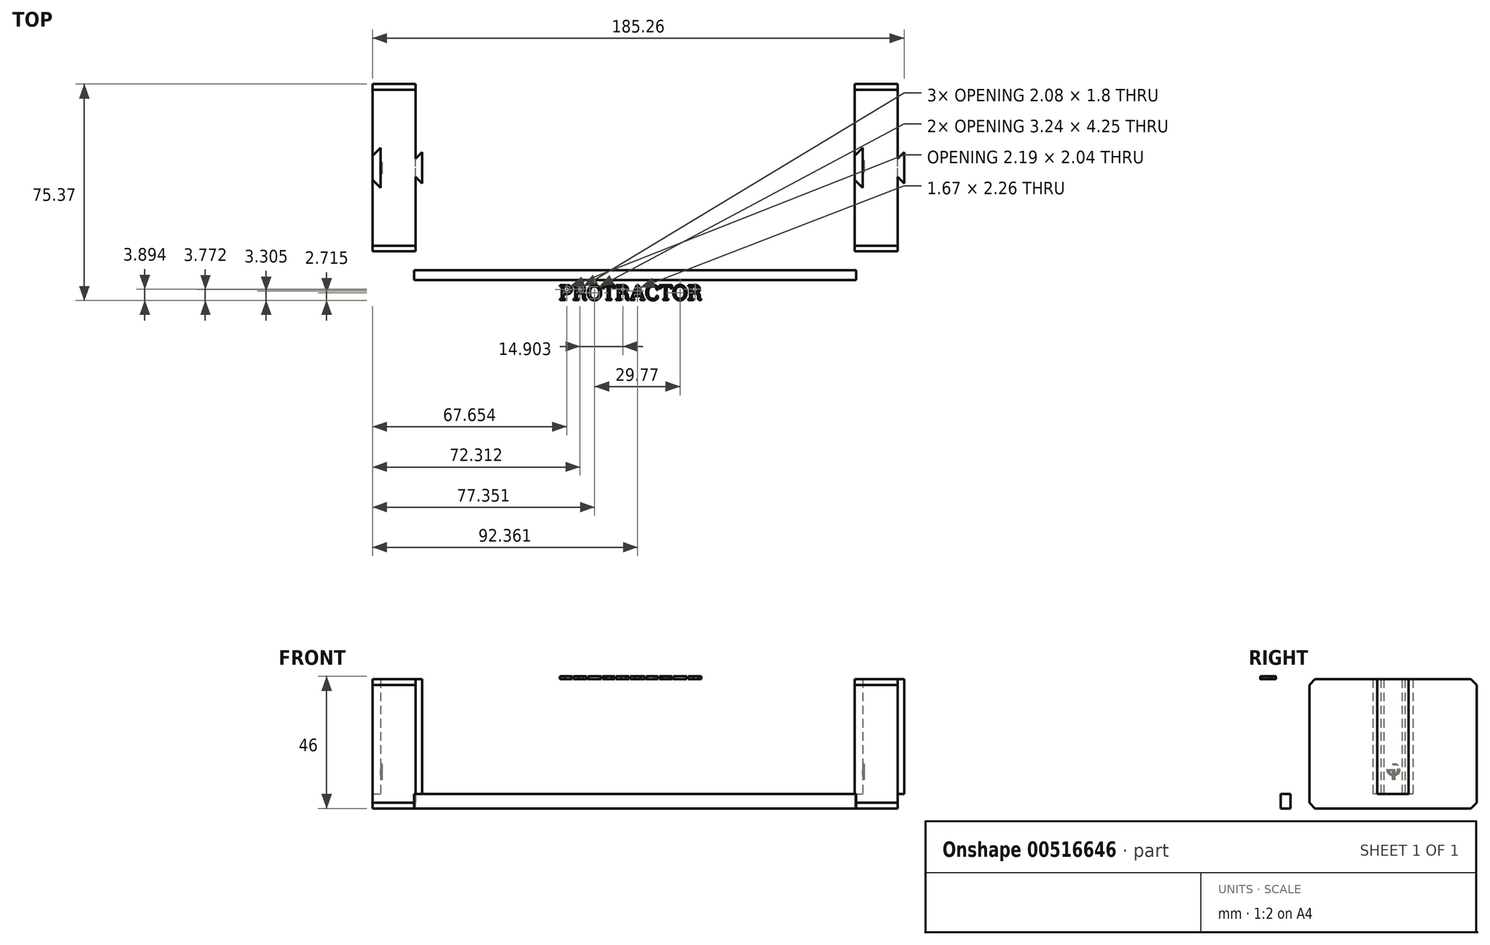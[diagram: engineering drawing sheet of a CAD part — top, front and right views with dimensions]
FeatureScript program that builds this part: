
annotation { "Feature Type Name" : "Feature", "Feature Type Description" : "" }
export const myFeature = defineFeature(function(context is Context, id is Id, definition is map)
    precondition{}
    {
        {
            var Q0;
            Q0=qCreatedBy(makeId("Top.planeOp"),FACE);
            var sketch = newSketch(context, id + "F0", { "sketchPlane" : qUnion([Q0])});
            skLineSegment(sketch, "E0", {"start": v(-15, 4.17) * mm, "end": v(-15, 29.17) * mm});
            skLineSegment(sketch, "E1", {"start": v(-15, 29.17) * mm, "end": v(0, 29.17) * mm});
            skLineSegment(sketch, "E2", {"start": v(0, 29.17) * mm, "end": v(0, 3.17) * mm});
            skLineSegment(sketch, "E3", {"start": v(-15, 4.17) * mm, "end": v(-12.17, 7) * mm});
            skLineSegment(sketch, "E4", {"start": v(-12.17, 7) * mm, "end": v(-12.17, 0) * mm});
            skLineSegment(sketch, "E5", {"start": v(0, 3.17) * mm, "end": v(2.26, 5.43) * mm});
            skLineSegment(sketch, "E6", {"start": v(2.26, 5.43) * mm, "end": v(2.26, -0.57) * mm});
            skLineSegment(sketch, "E7.MirrorCS", {"start": v(-15, -4.12) * mm, "end": v(-12.17, -6.95) * mm});
            skLineSegment(sketch, "E8.MirrorCS", {"start": v(0, -29.12) * mm, "end": v(0, -3.12) * mm});
            skLineSegment(sketch, "E9.MirrorCS", {"start": v(-12.17, -6.95) * mm, "end": v(-12.17, 0.05) * mm});
            skLineSegment(sketch, "E10.MirrorCS", {"start": v(-15, -4.12) * mm, "end": v(-15, -29.12) * mm});
            skLineSegment(sketch, "E11.MirrorCS", {"start": v(2.26, -5.39) * mm, "end": v(2.26, 0.61) * mm});
            skLineSegment(sketch, "E12.MirrorCS", {"start": v(0, -3.12) * mm, "end": v(2.26, -5.39) * mm});
            skLineSegment(sketch, "E13", {"start": v(153, 4.17) * mm, "end": v(153, 29.17) * mm});
            skLineSegment(sketch, "E14", {"start": v(153, 29.17) * mm, "end": v(168, 29.17) * mm});
            skLineSegment(sketch, "E15", {"start": v(168, 29.17) * mm, "end": v(168, 3.17) * mm});
            skLineSegment(sketch, "E16", {"start": v(153, 4.17) * mm, "end": v(155.83, 7) * mm});
            skLineSegment(sketch, "E17", {"start": v(155.83, 7) * mm, "end": v(155.83, 0) * mm});
            skLineSegment(sketch, "E18", {"start": v(168, 3.17) * mm, "end": v(170.26, 5.43) * mm});
            skLineSegment(sketch, "E19", {"start": v(170.26, 5.43) * mm, "end": v(170.26, -0.57) * mm});
            skLineSegment(sketch, "E20.MirrorCS", {"start": v(153, -4.17) * mm, "end": v(155.83, -7) * mm});
            skLineSegment(sketch, "E21.MirrorCS", {"start": v(168, -29.17) * mm, "end": v(168, -3.17) * mm});
            skLineSegment(sketch, "E22.MirrorCS", {"start": v(155.83, -7) * mm, "end": v(155.83, 0) * mm});
            skLineSegment(sketch, "E23.MirrorCS", {"start": v(153, -4.17) * mm, "end": v(153, -29.17) * mm});
            skLineSegment(sketch, "E24.MirrorCS", {"start": v(170.26, -5.43) * mm, "end": v(170.26, 0.57) * mm});
            skLineSegment(sketch, "E25.MirrorCS", {"start": v(168, -3.17) * mm, "end": v(170.26, -5.43) * mm});
            skLineSegment(sketch, "E26.bottom", {"start": v(-15, -29.12) * mm, "end": v(168, -29.12) * mm});
            skLineSegment(sketch, "E26.top", {"start": v(-15, -49.12) * mm, "end": v(168, -49.12) * mm});
            skLineSegment(sketch, "E26.left", {"start": v(-15, -29.12) * mm, "end": v(-15, -49.12) * mm});
            skLineSegment(sketch, "E26.right", {"start": v(168, -29.12) * mm, "end": v(168, -49.12) * mm});
            skLineSegment(sketch, "E27.bottom", {"start": v(-0.5, -35.62) * mm, "end": v(153.5, -35.62) * mm});
            skLineSegment(sketch, "E27.top", {"start": v(-0.5, -39.12) * mm, "end": v(153.5, -39.12) * mm});
            skLineSegment(sketch, "E27.left", {"start": v(-0.5, -35.62) * mm, "end": v(-0.5, -39.12) * mm});
            skLineSegment(sketch, "E27.right", {"start": v(153.5, -35.62) * mm, "end": v(153.5, -39.12) * mm});
            skLineSegment(sketch, "E28", {"start": v(-15, 4.17) * mm, "end": v(-15, -4.12) * mm});
            skLineSegment(sketch, "E29", {"start": v(153, -4.17) * mm, "end": v(153, 4.17) * mm});
            skLineSegment(sketch, "E30", {"start": v(0, 3.17) * mm, "end": v(0, -3.12) * mm});
            skLineSegment(sketch, "E31", {"start": v(168, 3.17) * mm, "end": v(168, -3.17) * mm});
            skSolve(sketch);
        }
        {
            var Q0;
            Q0=makeQuery(id+"F0.imprint","IMPRINT",FACE,{"disambiguationData":[TD([[makeQuery(id+"F0.imprint","IMPRINT",EDGE,{"derivedFrom":sQuery(id+"F0.wireOp",EDGE,"E5")}),-1.0]])]});
            var Q1;
            Q1=makeQuery(id+"F0.imprint","IMPRINT",FACE,{"disambiguationData":[TD([[makeQuery(id+"F0.imprint","IMPRINT",EDGE,{"derivedFrom":sQuery(id+"F0.wireOp",EDGE,"E18")}),-1.0]])]});
            var Q2;
            Q2=makeQuery(id+"F0.imprint","IMPRINT",FACE,{"disambiguationData":[TD([[makeQuery(id+"F0.imprint","IMPRINT",EDGE,{"derivedFrom":sQuery(id+"F0.wireOp",EDGE,"E0")}),-1.0]])]});
            var Q3;
            Q3=makeQuery(id+"F0.imprint","IMPRINT",FACE,{"disambiguationData":[TD([[makeQuery(id+"F0.imprint","IMPRINT",EDGE,{"derivedFrom":sQuery(id+"F0.wireOp",EDGE,"E13")}),-1.0]])]});
            var Q4;
            {var subQ0=sQuery(id+"F0.wireOp",EDGE,"E26.top");Q4=makeQuery(id+"F0.imprint","IMPRINT",FACE,{"disambiguationData":[TD([[makeQuery(id+"F0.imprint","IMPRINT",EDGE,{"derivedFrom":subQ0}),1.0]])]});}
            extrude(context, id + "F1", {"entities" : qUnion([Q0, Q1, Q2, Q3, Q4]), "depth" : 40 * mm, "offsetDistance" : 25 * mm});
        }
        {
            var Q0;
            Q0=makeQuery(id+"F0.imprint","IMPRINT",FACE,{"disambiguationData":[TD([[makeQuery(id+"F0.imprint","IMPRINT",EDGE,{"derivedFrom":sQuery(id+"F0.wireOp",EDGE,"E0")}),-1.0]])]});
            var Q1;
            Q1=makeQuery(id+"F0.imprint","IMPRINT",FACE,{"disambiguationData":[TD([[makeQuery(id+"F0.imprint","IMPRINT",EDGE,{"derivedFrom":sQuery(id+"F0.wireOp",EDGE,"E13")}),-1.0]])]});
            var Q2;
            Q2=makeQuery(id+"F0.imprint","IMPRINT",FACE,{"disambiguationData":[TD([[makeQuery(id+"F0.imprint","IMPRINT",EDGE,{"derivedFrom":sQuery(id+"F0.wireOp",EDGE,"E27.bottom")}),-1.0]])]});
            var Q3;
            {var subQ0=sQuery(id+"F0.wireOp",EDGE,"E26.top");Q3=makeQuery(id+"F0.imprint","IMPRINT",FACE,{"disambiguationData":[TD([[makeQuery(id+"F0.imprint","IMPRINT",EDGE,{"derivedFrom":subQ0}),1.0]])]});}
            var Q4;
            Q4=makeQuery(id+"F0.imprint","IMPRINT",FACE,{"disambiguationData":[TD([[makeQuery(id+"F0.imprint","IMPRINT",EDGE,{"derivedFrom":sQuery(id+"F0.wireOp",EDGE,"E3")}),-1.0]])]});
            var Q5;
            Q5=makeQuery(id+"F0.imprint","IMPRINT",FACE,{"disambiguationData":[TD([[makeQuery(id+"F0.imprint","IMPRINT",EDGE,{"derivedFrom":sQuery(id+"F0.wireOp",EDGE,"E16")}),-1.0]])]});
            extrude(context, id + "F2", {"entities" : qUnion([Q0, Q1, Q2, Q3, Q4, Q5]), "operationType" : NewBodyOperationType.ADD, "oppositeDirection" : true, "depth" : 5 * mm, "offsetDistance" : 25 * mm});
        }
        {
            var Q0;
            Q0=makeQuery(id+"F1.opExtrude","CAP_FACE",FACE,{"disambiguationData":[OSD([sQuery(id+"F0.wireOp",EDGE,"E0"),sQuery(id+"F0.wireOp",EDGE,"E1"),sQuery(id+"F0.wireOp",EDGE,"E2"),sQuery(id+"F0.wireOp",EDGE,"E3"),sQuery(id+"F0.wireOp",EDGE,"E4"),sQuery(id+"F0.wireOp",EDGE,"E5"),sQuery(id+"F0.wireOp",EDGE,"E6"),sQuery(id+"F0.wireOp",EDGE,"E7.MirrorCS"),sQuery(id+"F0.wireOp",EDGE,"E8.MirrorCS"),sQuery(id+"F0.wireOp",EDGE,"E9.MirrorCS"),sQuery(id+"F0.wireOp",EDGE,"E10.MirrorCS"),sQuery(id+"F0.wireOp",EDGE,"E11.MirrorCS"),sQuery(id+"F0.wireOp",EDGE,"E12.MirrorCS"),sQuery(id+"F0.wireOp",EDGE,"4d0a05fa-104b-468e-bad1-6da2c3376b846.MirrorCS"),sQuery(id+"F0.wireOp",EDGE,"KJNpoHbQ-aakG-BKsl-bdhx-CXvc9NHGIqeu.bottom"),sQuery(id+"F0.wireOp",EDGE,"KJNpoHbQ-aakG-BKsl-bdhx-CXvc9NHGIqeu.top"),sQuery(id+"F0.wireOp",EDGE,"KJNpoHbQ-aakG-BKsl-bdhx-CXvc9NHGIqeu.left"),sQuery(id+"F0.wireOp",EDGE,"KJNpoHbQ-aakG-BKsl-bdhx-CXvc9NHGIqeu.right")])],"isStart":false});
            var sketch = newSketch(context, id + "F3", { "sketchPlane" : qUnion([Q0])});
            skText(sketch, "E32", { "text": "PROTRACTOR", "fontName": "RobotoSlab-Regular.ttf"});
            const initialGuessF3  = {"E32": [0.05, -0.04612, 1, 0, 0.00534]};
            skSetInitialGuess(sketch, initialGuessF3);
            skSolve(sketch);
        }
        {
            var Q0;
            Q0=qSketchRegion(id+"F3",true);
            extrude(context, id + "F4", {"entities" : qUnion([Q0]), "operationType" : NewBodyOperationType.ADD, "depth" : 1 * mm});
        }
        {
            var Q0;
            Q0=makeQuery(id+"F1.opExtrude","CAP_EDGE",EDGE,{"disambiguationData":[OSD([sQuery(id+"F0.wireOp",EDGE,"E26.top")])],"isStart":false});
            var Q1;
            Q1=makeQuery(id+"F1.opExtrude","CAP_EDGE",EDGE,{"disambiguationData":[OSD([sQuery(id+"F0.wireOp",EDGE,"E1")])],"isStart":false});
            var Q2;
            Q2=makeQuery(id+"F1.opExtrude","CAP_EDGE",EDGE,{"disambiguationData":[OSD([sQuery(id+"F0.wireOp",EDGE,"E14")])],"isStart":false});
            var Q3;
            Q3=makeQuery(id+"F1.opExtrude","CAP_EDGE",EDGE,{"disambiguationData":[OSD([sQuery(id+"F0.wireOp",EDGE,"E26.bottom")])],"isStart":false});
            var Q4;
            Q4=makeQuery(id+"F2.opExtrude","CAP_EDGE",EDGE,{"disambiguationData":[OSD([sQuery(id+"F0.wireOp",EDGE,"E26.top")])],"isStart":false});
            var Q5;
            Q5=makeQuery(id+"F2.opExtrude","CAP_EDGE",EDGE,{"disambiguationData":[OSD([sQuery(id+"F0.wireOp",EDGE,"E26.bottom")])],"isStart":false});
            var Q6;
            Q6=makeQuery(id+"F2.opExtrude","CAP_EDGE",EDGE,{"disambiguationData":[OSD([sQuery(id+"F0.wireOp",EDGE,"E14")])],"isStart":false});
            var Q7;
            Q7=makeQuery(id+"F2.opExtrude","CAP_EDGE",EDGE,{"disambiguationData":[OSD([sQuery(id+"F0.wireOp",EDGE,"E1")])],"isStart":false});
            chamfer(context, id + "F5", {"entities" : qUnion([Q0, Q1, Q2, Q3, Q4, Q5, Q6, Q7]), "width" : 2 * mm, "tangentPropagation" : true});
        }
        {
            var Q0;
            Q0=makeQuery(id+"F1.opExtrude","SWEPT_FACE",FACE,{"disambiguationData":[OSD([sQuery(id+"F0.wireOp",EDGE,"E4"),sQuery(id+"F0.wireOp",EDGE,"E9.MirrorCS")])]});
            var sketch = newSketch(context, id + "F6", { "sketchPlane" : qUnion([Q0])});
            skLineSegment(sketch, "E33.bottom", {"start": v(0.12, 10.5) * mm, "end": v(2.12, 10.5) * mm, "construction": true});
            skLineSegment(sketch, "E33.top", {"start": v(0.12, 8.5) * mm, "end": v(2.12, 8.5) * mm, "construction": true});
            skLineSegment(sketch, "E33.left", {"start": v(0.12, 10.5) * mm, "end": v(0.12, 8.5) * mm, "construction": true});
            skLineSegment(sketch, "E33.right", {"start": v(2.12, 10.5) * mm, "end": v(2.12, 8.5) * mm, "construction": true});
            skArc(sketch, "E34", {"start": v(0.12, 10.5) * mm, "mid": v(-1.3, 7.09) * mm, "end": v(2.12, 8.5) * mm});
            skLineSegment(sketch, "E35", {"start": v(0.12, 10.5) * mm, "end": v(0.12, 10.25) * mm});
            skLineSegment(sketch, "E36", {"start": v(2.12, 8.5) * mm, "end": v(1.87, 8.5) * mm});
            skArc(sketch, "E37", {"start": v(0.12, 10.25) * mm, "mid": v(-1.12, 7.26) * mm, "end": v(1.87, 8.5) * mm});
            skLineSegment(sketch, "E38", {"start": v(1.87, 8.5) * mm, "end": v(0, 8.5) * mm});
            skLineSegment(sketch, "E39", {"start": v(0, 8.5) * mm, "end": v(0, 5) * mm});
            skLineSegment(sketch, "E40", {"start": v(0, 5) * mm, "end": v(0.25, 5) * mm});
            skLineSegment(sketch, "E41", {"start": v(1.85, 8.25) * mm, "end": v(0.25, 8.25) * mm});
            skLineSegment(sketch, "E42", {"start": v(0.25, 8.25) * mm, "end": v(0.25, 5) * mm});
            skSolve(sketch);
        }
        {
            var Q0;
            {var subQ0=sQuery(id+"F6.wireOp",EDGE,"E35");Q0=makeQuery(id+"F6.imprint","IMPRINT",FACE,{"disambiguationData":[TD([[makeQuery(id+"F6.imprint","IMPRINT",EDGE,{"derivedFrom":subQ0}),-1.0]])]});}
            var Q1;
            {var subQ1=sQuery(id+"F6.wireOp",EDGE,"E38");Q1=makeQuery(id+"F6.imprint","IMPRINT",FACE,{"disambiguationData":[TD([[makeQuery(id+"F6.imprint","IMPRINT",EDGE,{"derivedFrom":subQ1}),1.0]])]});}
            var Q2;
            {var subQ1=sQuery(id+"F6.wireOp",EDGE,"E36");Q2=makeQuery(id+"F6.imprint","IMPRINT",FACE,{"disambiguationData":[TD([[makeQuery(id+"F6.imprint","IMPRINT",EDGE,{"derivedFrom":subQ1}),1.0]])]});}
            var Q3;
            {var subQ0=sQuery(id+"F6.wireOp",EDGE,"E39");var subQ1=sQuery(id+"F6.wireOp",EDGE,"E34");var subQ2=makeQuery(id+"F6.imprint","INTERSECT",VERTEX,{"derivedFrom":[subQ1,subQ0]});Q3=makeQuery(id+"F6.imprint","IMPRINT",FACE,{"disambiguationData":[TD([[makeQuery(id+"F6.imprint","IMPRINT",EDGE,{"disambiguationData":[TD([[subQ2,-1.0]])],"derivedFrom":subQ1}),1.0]])]});}
            var Q4;
            {var subQ5=sQuery(id+"F6.wireOp",EDGE,"E40");Q4=makeQuery(id+"F6.imprint","IMPRINT",FACE,{"disambiguationData":[TD([[makeQuery(id+"F6.imprint","IMPRINT",EDGE,{"derivedFrom":subQ5}),1.0]])]});}
            extrude(context, id + "F7", {"entities" : qUnion([Q0, Q1, Q2, Q3, Q4]), "operationType" : NewBodyOperationType.REMOVE, "oppositeDirection" : true, "depth" : .5 * mm, "offsetDistance" : 25 * mm});
        }
        {
            var Q0;
            Q0=makeQuery(id+"F1.opExtrude","SWEPT_FACE",FACE,{"disambiguationData":[OSD([sQuery(id+"F0.wireOp",EDGE,"E17"),sQuery(id+"F0.wireOp",EDGE,"E22.MirrorCS")])]});
            var sketch = newSketch(context, id + "F8", { "sketchPlane" : qUnion([Q0])});
            skLineSegment(sketch, "E43.bottom", {"start": v(-0.52, 10.5) * mm, "end": v(1.48, 10.5) * mm, "construction": true});
            skLineSegment(sketch, "E43.top", {"start": v(-0.52, 8.5) * mm, "end": v(1.48, 8.5) * mm, "construction": true});
            skLineSegment(sketch, "E43.left", {"start": v(-0.52, 10.5) * mm, "end": v(-0.52, 8.5) * mm, "construction": true});
            skLineSegment(sketch, "E43.right", {"start": v(1.48, 10.5) * mm, "end": v(1.48, 8.5) * mm, "construction": true});
            skArc(sketch, "E44", {"start": v(-0.52, 10.5) * mm, "mid": v(-1.93, 7.09) * mm, "end": v(1.48, 8.5) * mm});
            skLineSegment(sketch, "E45", {"start": v(-0.52, 10.5) * mm, "end": v(-0.52, 10.25) * mm});
            skLineSegment(sketch, "E46", {"start": v(1.48, 8.5) * mm, "end": v(1.23, 8.5) * mm});
            skArc(sketch, "E47", {"start": v(-0.52, 10.25) * mm, "mid": v(-1.75, 7.26) * mm, "end": v(1.23, 8.5) * mm});
            skLineSegment(sketch, "E48", {"start": v(1.23, 8.5) * mm, "end": v(-0.64, 8.5) * mm});
            skLineSegment(sketch, "E49", {"start": v(-0.64, 8.5) * mm, "end": v(-0.64, 5) * mm});
            skLineSegment(sketch, "E50", {"start": v(-0.64, 5) * mm, "end": v(-0.39, 5) * mm});
            skLineSegment(sketch, "E51", {"start": v(1.22, 8.25) * mm, "end": v(-0.39, 8.25) * mm});
            skLineSegment(sketch, "E52", {"start": v(-0.39, 8.25) * mm, "end": v(-0.39, 5) * mm});
            skSolve(sketch);
        }
        {
            var Q0;
            {var subQ0=sQuery(id+"F8.wireOp",EDGE,"E45");Q0=makeQuery(id+"F8.imprint","IMPRINT",FACE,{"disambiguationData":[TD([[makeQuery(id+"F8.imprint","IMPRINT",EDGE,{"derivedFrom":subQ0}),-1.0]])]});}
            var Q1;
            {var subQ1=sQuery(id+"F8.wireOp",EDGE,"E48");Q1=makeQuery(id+"F8.imprint","IMPRINT",FACE,{"disambiguationData":[TD([[makeQuery(id+"F8.imprint","IMPRINT",EDGE,{"derivedFrom":subQ1}),1.0]])]});}
            var Q2;
            {var subQ5=sQuery(id+"F8.wireOp",EDGE,"E50");Q2=makeQuery(id+"F8.imprint","IMPRINT",FACE,{"disambiguationData":[TD([[makeQuery(id+"F8.imprint","IMPRINT",EDGE,{"derivedFrom":subQ5}),1.0]])]});}
            var Q3;
            {var subQ1=sQuery(id+"F8.wireOp",EDGE,"E46");Q3=makeQuery(id+"F8.imprint","IMPRINT",FACE,{"disambiguationData":[TD([[makeQuery(id+"F8.imprint","IMPRINT",EDGE,{"derivedFrom":subQ1}),1.0]])]});}
            var Q4;
            {var subQ0=sQuery(id+"F8.wireOp",EDGE,"E49");var subQ1=sQuery(id+"F8.wireOp",EDGE,"E44");var subQ2=makeQuery(id+"F8.imprint","INTERSECT",VERTEX,{"derivedFrom":[subQ1,subQ0]});Q4=makeQuery(id+"F8.imprint","IMPRINT",FACE,{"disambiguationData":[TD([[makeQuery(id+"F8.imprint","IMPRINT",EDGE,{"disambiguationData":[TD([[subQ2,-1.0]])],"derivedFrom":subQ1}),1.0]])]});}
            extrude(context, id + "F9", {"entities" : qUnion([Q0, Q1, Q2, Q3, Q4]), "operationType" : NewBodyOperationType.REMOVE, "oppositeDirection" : true, "depth" : .5 * mm, "offsetDistance" : 25 * mm});
        }
    });
